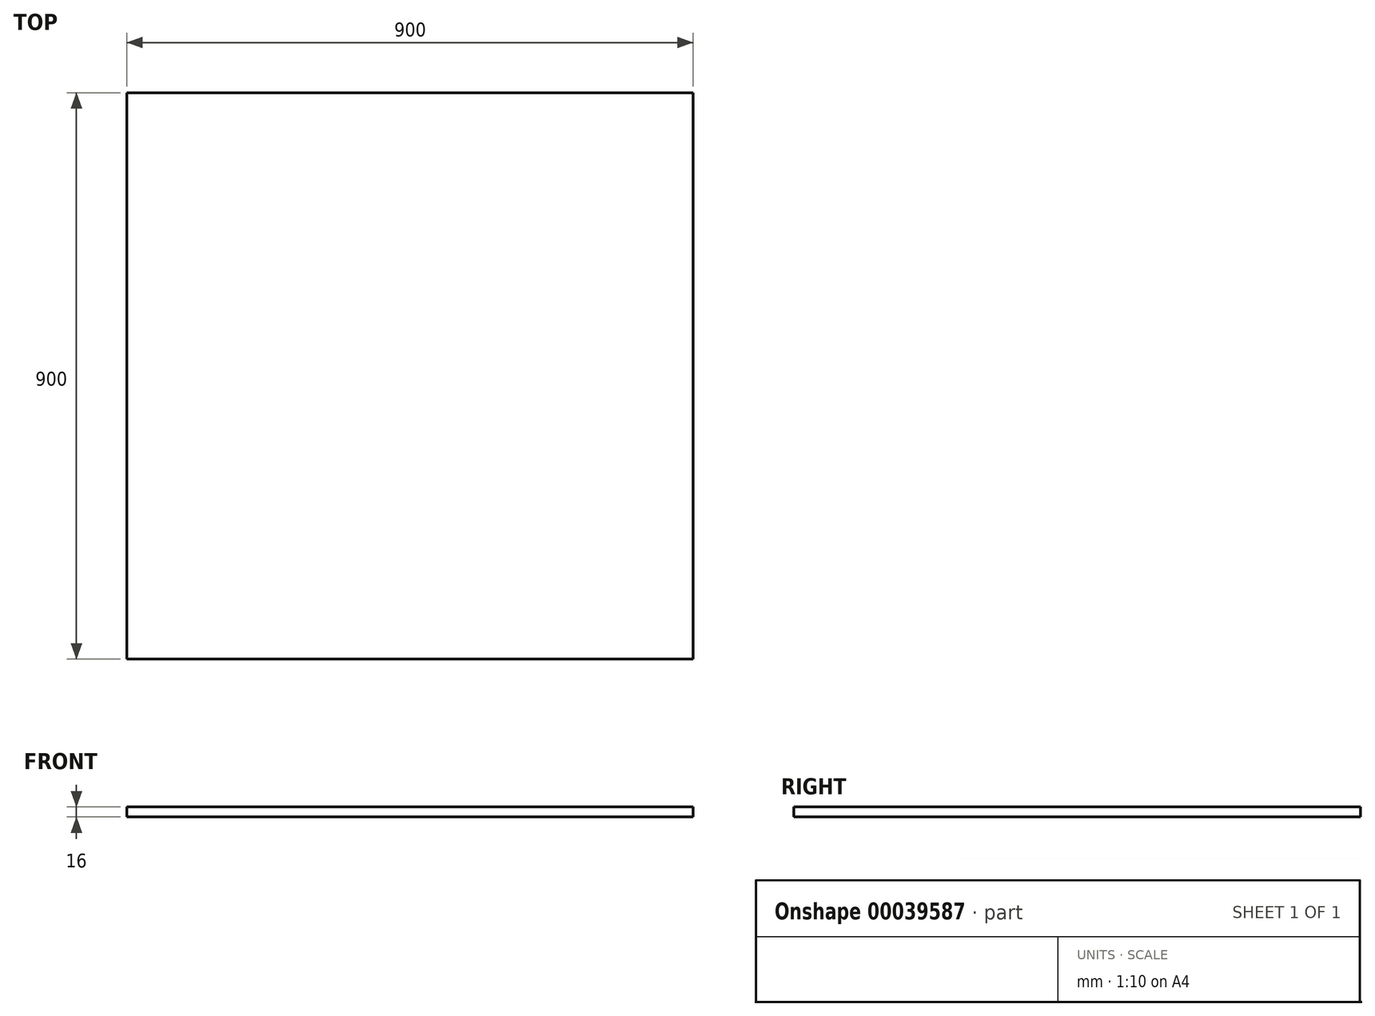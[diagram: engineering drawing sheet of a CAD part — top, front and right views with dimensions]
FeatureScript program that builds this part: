
annotation { "Feature Type Name" : "Feature", "Feature Type Description" : "" }
export const myFeature = defineFeature(function(context is Context, id is Id, definition is map)
    precondition{}
    {
        {
            var Q0;
            Q0=qCreatedBy(makeId("Top.planeOp"),FACE);
            var sketch = newSketch(context, id + "F0", { "sketchPlane" : qUnion([Q0])});
            skLineSegment(sketch, "E0.bottom", {"start": v(-54.56, 874.45) * mm, "end": v(845.44, 874.45) * mm});
            skLineSegment(sketch, "E0.top", {"start": v(-54.56, -25.55) * mm, "end": v(845.44, -25.55) * mm});
            skLineSegment(sketch, "E0.left", {"start": v(-54.56, 874.45) * mm, "end": v(-54.56, -25.55) * mm});
            skLineSegment(sketch, "E0.right", {"start": v(845.44, 874.45) * mm, "end": v(845.44, -25.55) * mm});
            skSolve(sketch);
        }
        {
            var Q0;
            Q0 = qSketchRegion(id + "F0", true);
            extrude(context, id + "F1", {"entities" : qUnion([Q0]), "depth" : 16 * mm});
        }
    });
